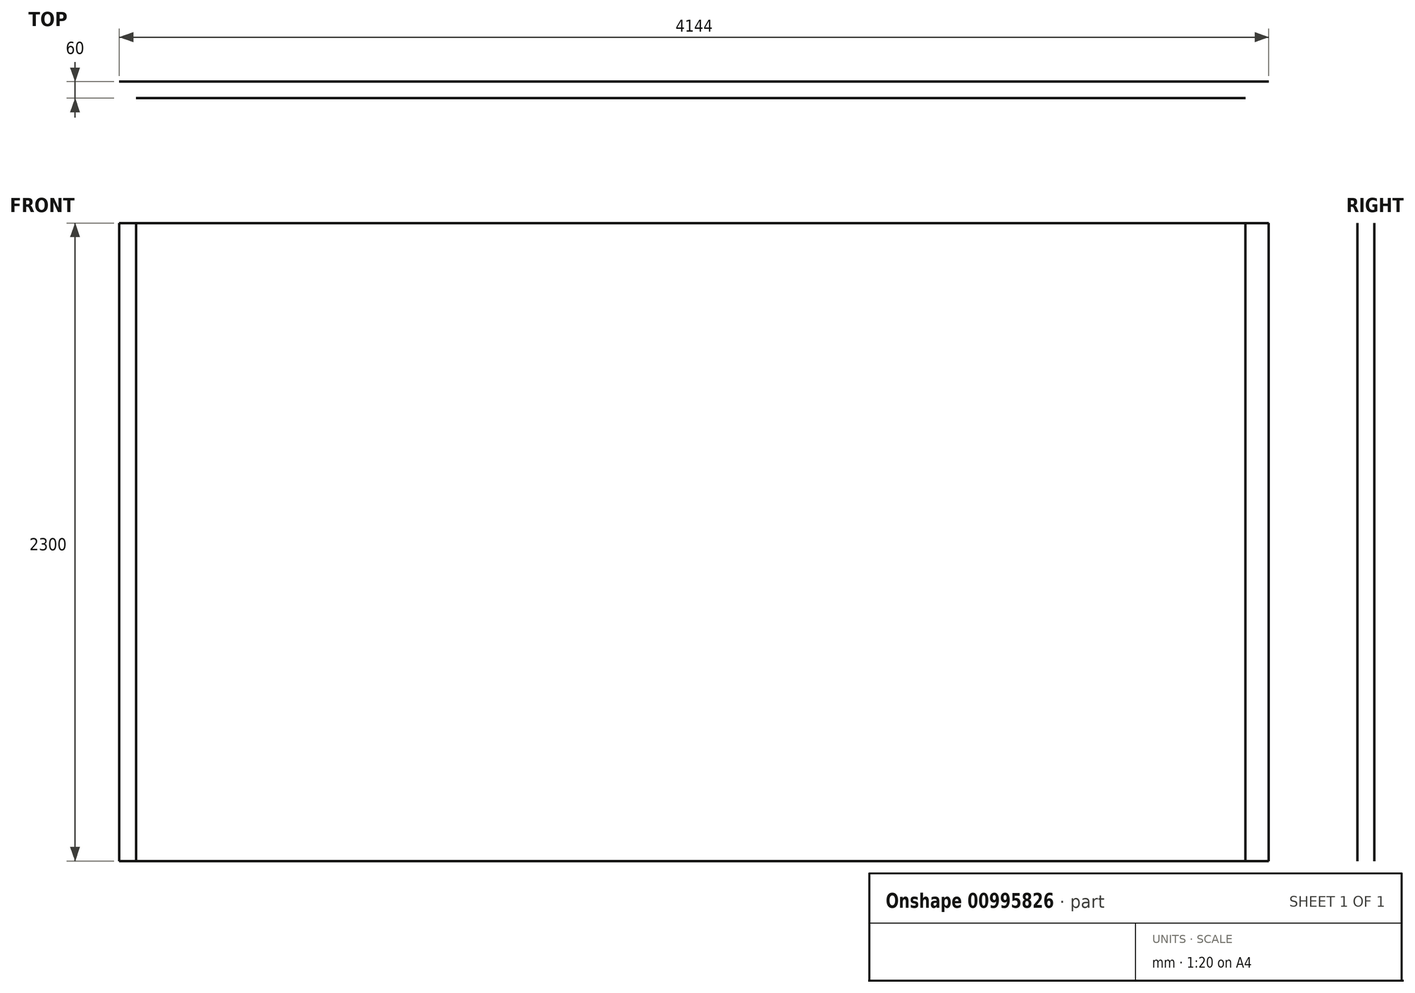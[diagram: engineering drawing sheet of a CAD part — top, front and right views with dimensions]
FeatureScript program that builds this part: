
annotation { "Feature Type Name" : "Feature", "Feature Type Description" : "" }
export const myFeature = defineFeature(function(context is Context, id is Id, definition is map)
    precondition{}
    {
        {
            var Q0;
            Q0=qCreatedBy(makeId("Top.planeOp"),FACE);
            var sketch = newSketch(context, id + "F0", { "sketchPlane" : qUnion([Q0])});
            skLineSegment(sketch, "E0", {"start": v(0, 0) * mm, "end": v(0, -3500) * mm});
            skLineSegment(sketch, "E1", {"start": v(0, 0) * mm, "end": v(4000, 0) * mm});
            skLineSegment(sketch, "E2", {"start": v(4000, 0) * mm, "end": v(2800, -3500) * mm});
            skLineSegment(sketch, "E3", {"start": v(2800, -3500) * mm, "end": v(0, -3500) * mm});
            skLineSegment(sketch, "E4.0", {"start": v(2842.86, -3560) * mm, "end": v(-60, -3560) * mm});
            skLineSegment(sketch, "E4.1", {"start": v(4084, 60) * mm, "end": v(2842.86, -3560) * mm});
            skLineSegment(sketch, "E4.2", {"start": v(-60, 60) * mm, "end": v(4084, 60) * mm});
            skLineSegment(sketch, "E4.3", {"start": v(-60, 60) * mm, "end": v(-60, -3560) * mm});
            skSolve(sketch);
        }
        {
            var Q0;
            Q0=sQuery(id+"F0.wireOp",EDGE,"E4.2");
            var Q1;
            Q1=sQuery(id+"F0.wireOp",EDGE,"E1");
            extrude(context, id + "F1", {"bodyType" : ToolBodyType.SURFACE, "surfaceEntities" : qUnion([Q0, Q1]), "depth" : 2300 * mm, "offsetDistance" : 25 * mm});
        }
    });
